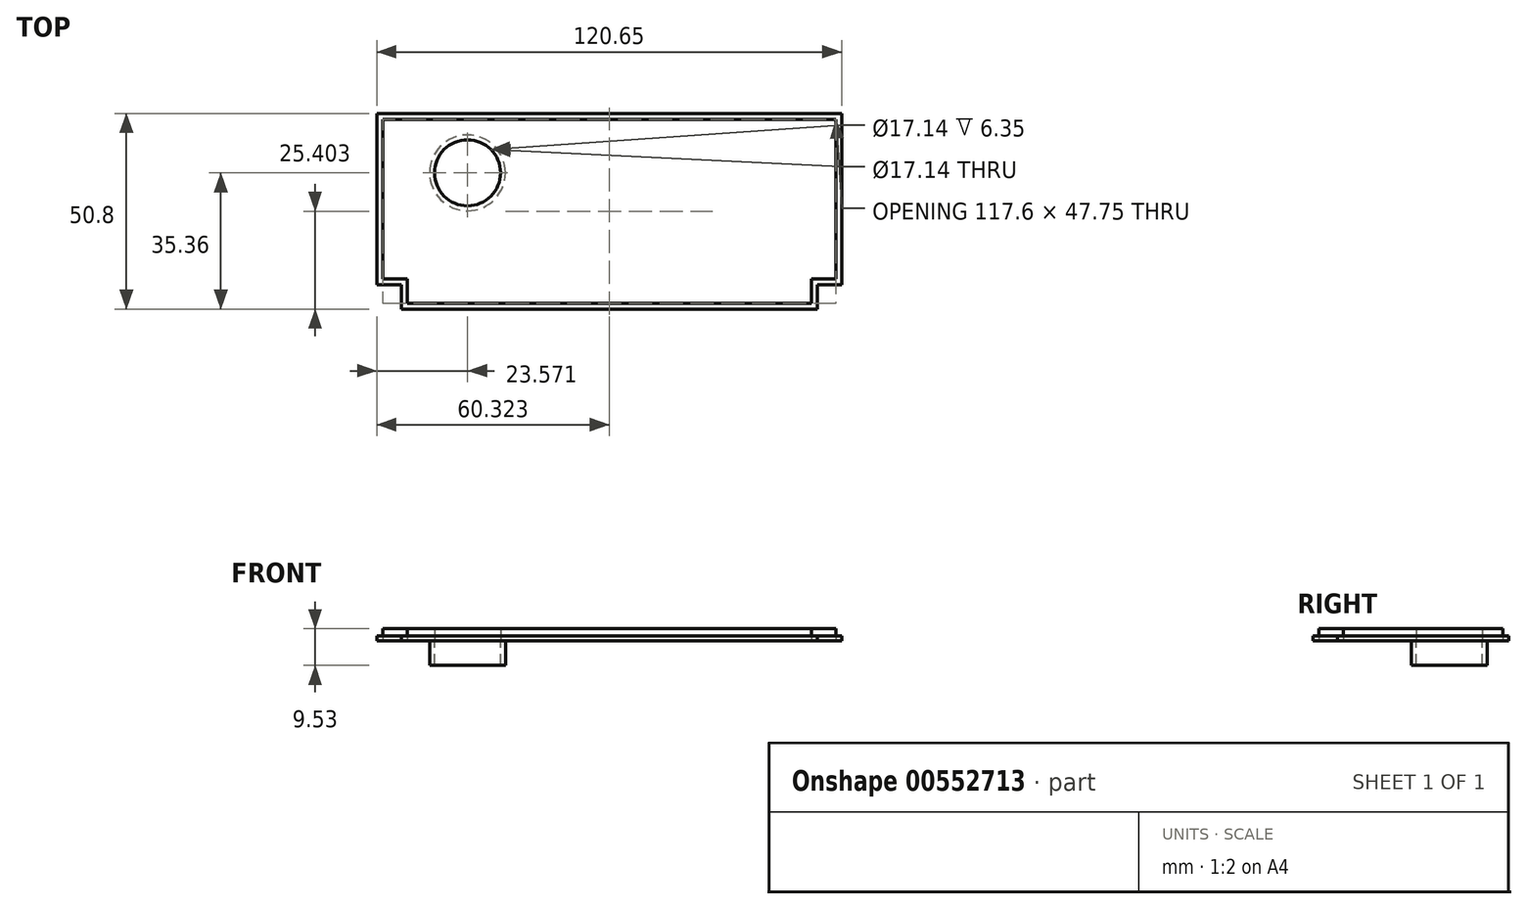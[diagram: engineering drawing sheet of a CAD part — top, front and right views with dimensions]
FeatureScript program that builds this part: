
annotation { "Feature Type Name" : "Feature", "Feature Type Description" : "" }
export const myFeature = defineFeature(function(context is Context, id is Id, definition is map)
    precondition{}
    {
        {
            var Q0;
            Q0=qCreatedBy(makeId("Top.planeOp"),FACE);
            var sketch = newSketch(context, id + "F0", { "sketchPlane" : qUnion([Q0])});
            skLineSegment(sketch, "E0", {"start": v(-47.3, 27.34) * mm, "end": v(73.36, 27.34) * mm});
            skLineSegment(sketch, "E1", {"start": v(73.36, 27.34) * mm, "end": v(73.36, -17.1) * mm});
            skLineSegment(sketch, "E2", {"start": v(73.36, -17.1) * mm, "end": v(67, -17.1) * mm});
            skLineSegment(sketch, "E3", {"start": v(67, -17.1) * mm, "end": v(67, -23.46) * mm});
            skLineSegment(sketch, "E4", {"start": v(67, -23.46) * mm, "end": v(-40.94, -23.46) * mm});
            skLineSegment(sketch, "E5", {"start": v(-40.94, -23.46) * mm, "end": v(-40.94, -17.1) * mm});
            skLineSegment(sketch, "E6", {"start": v(-40.94, -17.1) * mm, "end": v(-47.3, -17.1) * mm});
            skLineSegment(sketch, "E7", {"start": v(-47.3, -17.1) * mm, "end": v(-47.3, 27.34) * mm});
            skCircle(sketch, "E8", {"center": v(-23.72, 11.9) * mm, "radius": 8.57 * mm});
            skLineSegment(sketch, "E9", {"start": v(-45.77, -15.58) * mm, "end": v(-39.42, -15.58) * mm});
            skLineSegment(sketch, "E10", {"start": v(-39.42, -15.58) * mm, "end": v(-39.42, -21.93) * mm});
            skLineSegment(sketch, "E11", {"start": v(-39.42, -21.93) * mm, "end": v(65.48, -21.93) * mm});
            skLineSegment(sketch, "E12", {"start": v(65.48, -21.93) * mm, "end": v(65.48, -15.58) * mm});
            skLineSegment(sketch, "E13", {"start": v(65.48, -15.58) * mm, "end": v(71.83, -15.58) * mm});
            skLineSegment(sketch, "E14", {"start": v(71.83, -15.58) * mm, "end": v(71.83, 25.82) * mm});
            skLineSegment(sketch, "E15", {"start": v(71.83, 25.82) * mm, "end": v(-45.77, 25.82) * mm});
            skLineSegment(sketch, "E16", {"start": v(-45.77, 25.82) * mm, "end": v(-45.77, -15.58) * mm});
            skCircle(sketch, "E17", {"center": v(-23.72, 11.9) * mm, "radius": 9.84 * mm});
            skSolve(sketch);
        }
        {
            var Q0;
            Q0=makeQuery(id+"F0.imprint","IMPRINT",FACE,{"disambiguationData":[TD([[makeQuery(id+"F0.imprint","IMPRINT",EDGE,{"derivedFrom":sQuery(id+"F0.wireOp",EDGE,"E8")}),-1.0]])]});
            var Q1;
            Q1=makeQuery(id+"F0.imprint","IMPRINT",FACE,{"disambiguationData":[TD([[makeQuery(id+"F0.imprint","IMPRINT",EDGE,{"derivedFrom":sQuery(id+"F0.wireOp",EDGE,"E9")}),1.0]])]});
            extrude(context, id + "F1", {"entities" : qUnion([Q0, Q1]), "depth" : 3.17 * mm, "offsetDistance" : 25.4 * mm});
        }
        {
            var Q0;
            Q0 = qSketchRegion(id + "F0", true);
            extrude(context, id + "F2", {"entities" : qUnion([Q0]), "depth" : 1.27 * mm, "offsetDistance" : 25.4 * mm});
        }
        {
            var Q0;
            Q0=makeQuery(id+"F0.imprint","IMPRINT",FACE,{"disambiguationData":[TD([[makeQuery(id+"F0.imprint","IMPRINT",EDGE,{"derivedFrom":sQuery(id+"F0.wireOp",EDGE,"E8")}),-1.0]])]});
            extrude(context, id + "F3", {"entities" : qUnion([Q0]), "oppositeDirection" : true, "depth" : 6.35 * mm, "offsetDistance" : 25.4 * mm});
        }
    });
